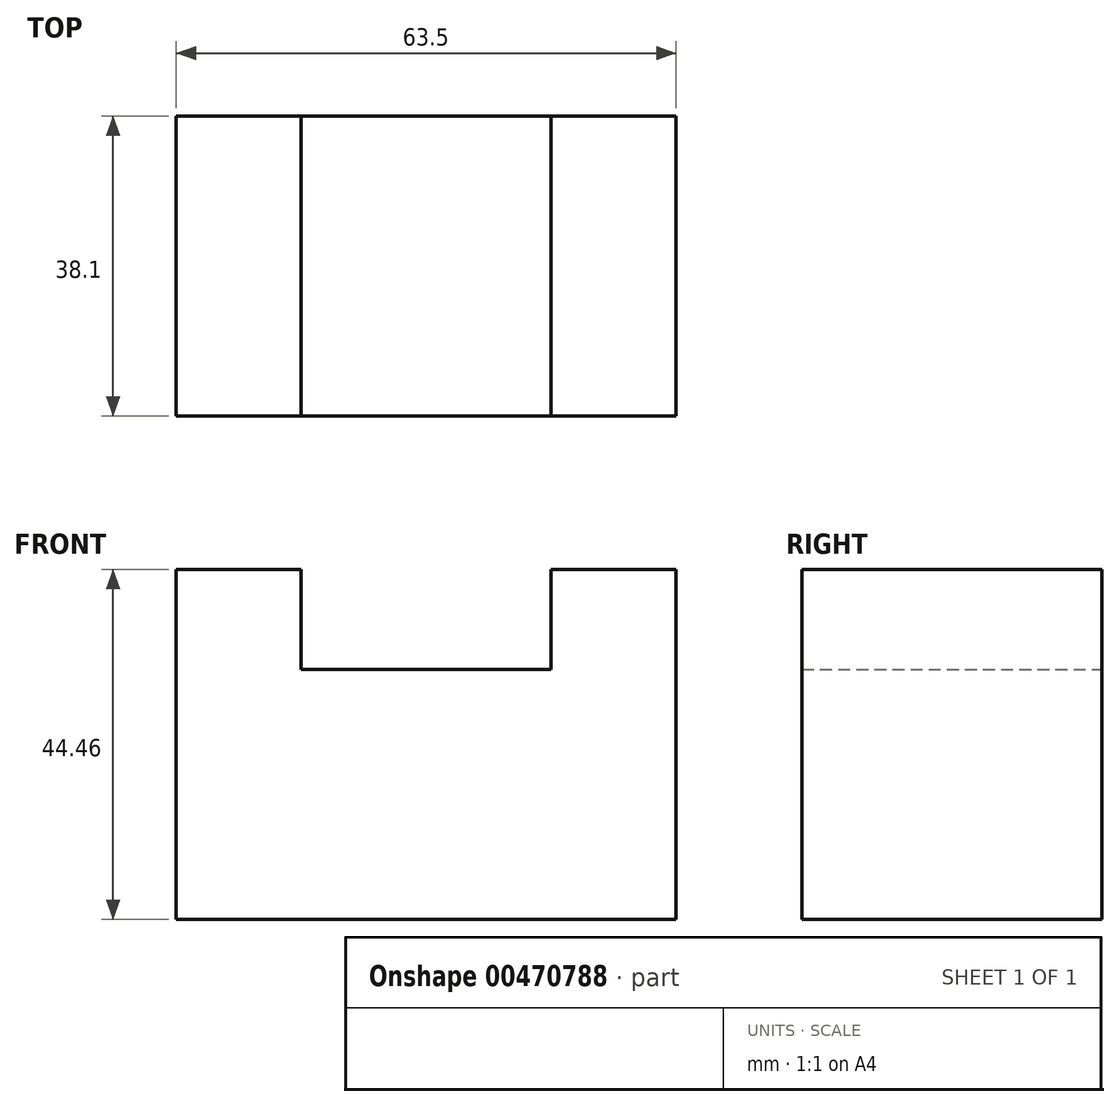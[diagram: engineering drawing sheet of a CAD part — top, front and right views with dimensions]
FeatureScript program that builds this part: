
annotation { "Feature Type Name" : "Feature", "Feature Type Description" : "" }
export const myFeature = defineFeature(function(context is Context, id is Id, definition is map)
    precondition{}
    {
        {
            var Q0;
            Q0=qCreatedBy(makeId("Front.planeOp"),FACE);
            var sketch = newSketch(context, id + "F0", { "sketchPlane" : qUnion([Q0])});
            skLineSegment(sketch, "E0.bottom", {"start": v(-31.75, 22.23) * mm, "end": v(31.75, 22.23) * mm});
            skLineSegment(sketch, "E0.top", {"start": v(-31.75, -22.23) * mm, "end": v(31.75, -22.23) * mm});
            skLineSegment(sketch, "E0.left", {"start": v(-31.75, 22.23) * mm, "end": v(-31.75, -22.23) * mm});
            skLineSegment(sketch, "E0.right", {"start": v(31.75, 22.23) * mm, "end": v(31.75, -22.22) * mm});
            skPoint(sketch, "E0.middle", {"position": v(0, 0) * mm});
            skLineSegment(sketch, "E1.bottom", {"start": v(-15.88, 22.23) * mm, "end": v(15.87, 22.23) * mm});
            skLineSegment(sketch, "E1.top", {"start": v(-15.88, 9.53) * mm, "end": v(15.87, 9.53) * mm});
            skLineSegment(sketch, "E1.left", {"start": v(-15.88, 22.23) * mm, "end": v(-15.88, 9.53) * mm});
            skLineSegment(sketch, "E1.right", {"start": v(15.87, 22.23) * mm, "end": v(15.87, 9.53) * mm});
            skSolve(sketch);
        }
        {
            var Q0;
            Q0=makeQuery(id+"F0.imprint","IMPRINT",FACE,{"disambiguationData":[TD([[makeQuery(id+"F0.imprint","IMPRINT",EDGE,{"derivedFrom":sQuery(id+"F0.wireOp",EDGE,"E0.top")}),1.0]])]});
            extrude(context, id + "F1", {"entities" : qUnion([Q0]), "depth" : 38.1 * mm});
        }
    });
